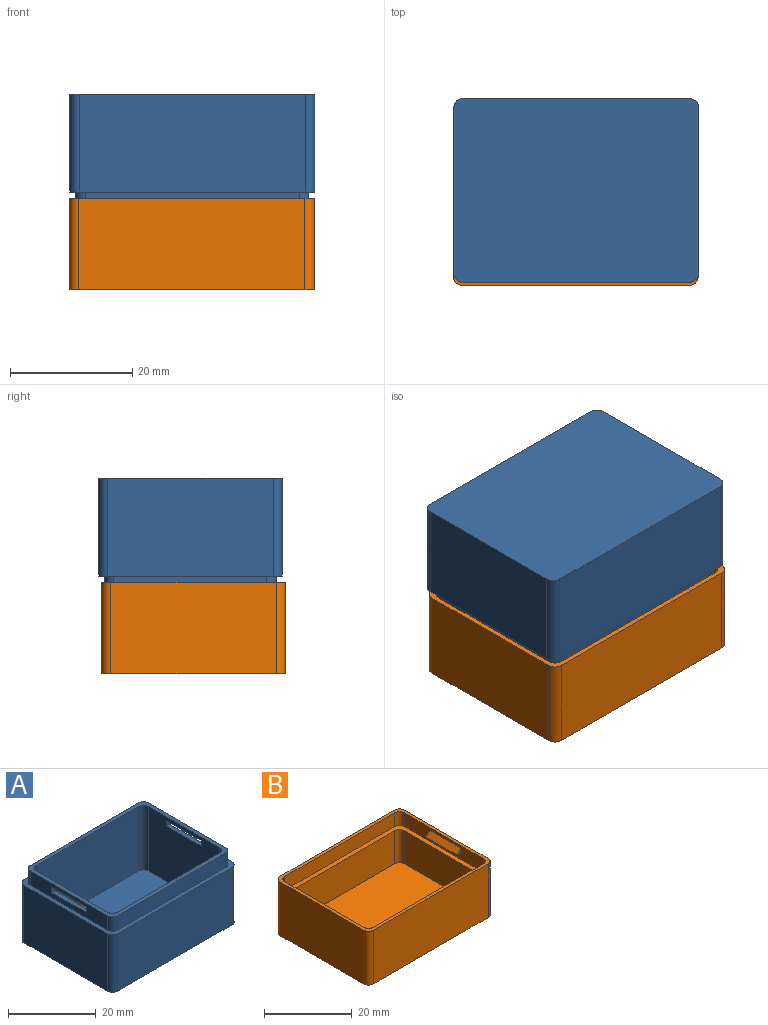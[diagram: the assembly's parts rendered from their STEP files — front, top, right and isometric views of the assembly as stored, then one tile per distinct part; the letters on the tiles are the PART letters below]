
ASSEMBLY  parts=2 mates=1
PART A: 36 faces, bbox 40x30x20 mm
  f0: plane 23x18mm, normal (1,0,0), area 397.5mm2, adj f4,f7,f10,f11,f32,f33,f34,f35
  f1: plane 23x18mm, normal (-1,0,0), area 397.5mm2, adj f4,f7,f8,f9,f28,f29,f30,f31
  f2: plane 25x4mm, normal (-1,0,0), area 83.5mm2, adj f4,f14,f24,f27,f32,f33,f34,f35
  f3: plane 25x4mm, normal (1,0,0), area 83.5mm2, adj f4,f14,f25,f26,f28,f29,f30,f31
  f4: plane 38x28mm, normal (0,0,1), area 128mm2, adj f0,f1,f2,f3,f5,f6,f8,f9
  f5: plane 33x18mm, normal (0,-1,0), area 594mm2, adj f4,f7,f9,f11
  f6: plane 33x18mm, normal (0,1,0), area 594mm2, adj f4,f7,f8,f10
  f7: plane 36x26mm, normal (0,0,1), area 934.1mm2, adj f0,f1,f5,f6,f8,f9,f10,f11
  f8: cylinder r=1.5mm len=18mm, axis (0,0,-1), area 42.4mm2, adj f1,f4,f6,f7
  f9: cylinder r=1.5mm len=18mm, axis (0,0,1), area 42.4mm2, adj f1,f4,f5,f7
  f10: cylinder r=1.5mm len=18mm, axis (0,0,1), area 42.4mm2, adj f0,f4,f6,f7
  f11: cylinder r=1.5mm len=18mm, axis (0,0,-1), area 42.4mm2, adj f0,f4,f5,f7
  f12: plane 35x4mm, normal (0,1,0), area 140mm2, adj f4,f14,f24,f25
  f13: plane 35x4mm, normal (0,-1,0), area 140mm2, adj f4,f14,f26,f27
  f14: plane 40x30mm, normal (0,0,1), area 136mm2, adj f2,f3,f12,f13,f16,f17,f18,f19
  f15: plane 40x30mm, normal (0,0,-1), area 1198.1mm2, adj f16,f17,f18,f19,f20,f21,f22,f23
  f16: cylinder r=1.5mm len=16mm, axis (0,0,1), area 37.7mm2, adj f14,f15,f18,f20
  f17: cylinder r=1.5mm len=16mm, axis (0,0,-1), area 37.7mm2, adj f14,f15,f18,f23
  f18: plane 27x16mm, normal (1,0,0), area 432mm2, adj f14,f15,f16,f17
  f19: cylinder r=1.5mm len=16mm, axis (0,0,-1), area 37.7mm2, adj f14,f15,f20,f22
  f20: plane 37x16mm, normal (0,-1,0), area 592mm2, adj f14,f15,f16,f19
  f21: cylinder r=1.5mm len=16mm, axis (0,0,1), area 37.7mm2, adj f14,f15,f22,f23
  f22: plane 27x16mm, normal (-1,0,0), area 432mm2, adj f14,f15,f19,f21
  f23: plane 37x16mm, normal (0,1,0), area 592mm2, adj f14,f15,f17,f21
  f24: cylinder r=1.5mm len=4mm, axis (0,0,-1), area 9.4mm2, adj f2,f4,f12,f14
  f25: cylinder r=1.5mm len=4mm, axis (0,0,1), area 9.4mm2, adj f3,f4,f12,f14
  f26: cylinder r=1.5mm len=4mm, axis (0,0,-1), area 9.4mm2, adj f3,f4,f13,f14
  f27: cylinder r=1.5mm len=4mm, axis (0,0,1), area 9.4mm2, adj f2,f4,f13,f14
  f28: plane 1.5x1mm, normal (0,-1,0), area 1.5mm2, adj f1,f3,f29,f31
  f29: plane 11x1mm, normal (0,0,1), area 11mm2, adj f1,f3,f28,f30
  f30: plane 1.5x1mm, normal (0,1,0), area 1.5mm2, adj f1,f3,f29,f31
  f31: plane 11x1mm, normal (0,0,-1), area 11mm2, adj f1,f3,f28,f30
  f32: plane 11x1mm, normal (0,0,-1), area 11mm2, adj f0,f2,f33,f35
  f33: plane 1.5x1mm, normal (0,1,0), area 1.5mm2, adj f0,f2,f32,f34
  f34: plane 11x1mm, normal (0,0,1), area 11mm2, adj f0,f2,f33,f35
  f35: plane 1.5x1mm, normal (0,-1,0), area 1.5mm2, adj f0,f2,f32,f34
PART B: 36 faces, bbox 40x30x15 mm
  f0: plane 25.4x3.8mm, normal (-1,0,0), area 83.5mm2, adj f2,f12,f26,f27,f32,f33,f34,f35
  f1: plane 25.4x3.8mm, normal (1,0,0), area 83.5mm2, adj f2,f12,f24,f25,f28,f29,f30,f31
  f2: plane 40x30mm, normal (0,0,1), area 109.4mm2, adj f0,f1,f3,f4,f5,f6,f8,f9
  f3: plane 37x15mm, normal (0,1,0), area 555mm2, adj f2,f7,f8,f11
  f4: plane 27x15mm, normal (-1,0,0), area 405mm2, adj f2,f7,f8,f9
  f5: plane 37x15mm, normal (0,-1,0), area 555mm2, adj f2,f7,f9,f10
  f6: plane 27x15mm, normal (1,0,0), area 405mm2, adj f2,f7,f10,f11
  f7: plane 40x30mm, normal (0,0,-1), area 1198.1mm2, adj f3,f4,f5,f6,f8,f9,f10,f11
  f8: cylinder r=1.5mm len=15mm, axis (0,0,1), area 35.3mm2, adj f2,f3,f4,f7
  f9: cylinder r=1.5mm len=15mm, axis (0,0,-1), area 35.3mm2, adj f2,f4,f5,f7
  f10: cylinder r=1.5mm len=15mm, axis (0,0,1), area 35.3mm2, adj f2,f5,f6,f7
  f11: cylinder r=1.5mm len=15mm, axis (0,0,-1), area 35.3mm2, adj f2,f3,f6,f7
  f12: plane 38.4x28.4mm, normal (0,0,1), area 154.6mm2, adj f0,f1,f13,f14,f16,f17,f18,f19
  f13: plane 35.4x3.8mm, normal (0,-1,0), area 134.5mm2, adj f2,f12,f24,f27
  f14: plane 35.4x3.8mm, normal (0,1,0), area 134.5mm2, adj f2,f12,f25,f26
  f15: plane 36x26mm, normal (0,0,1), area 934.1mm2, adj f16,f17,f18,f19,f20,f21,f22,f23
  f16: cylinder r=1.5mm len=9.2mm, axis (0,0,-1), area 21.7mm2, adj f12,f15,f18,f20
  f17: cylinder r=1.5mm len=9.2mm, axis (0,0,1), area 21.7mm2, adj f12,f15,f18,f23
  f18: plane 23x9.2mm, normal (-1,0,0), area 211.6mm2, adj f12,f15,f16,f17
  f19: cylinder r=1.5mm len=9.2mm, axis (0,0,1), area 21.7mm2, adj f12,f15,f20,f22
  f20: plane 33x9.2mm, normal (0,1,0), area 303.6mm2, adj f12,f15,f16,f19
  f21: cylinder r=1.5mm len=9.2mm, axis (0,0,-1), area 21.7mm2, adj f12,f15,f22,f23
  f22: plane 23x9.2mm, normal (1,0,0), area 211.6mm2, adj f12,f15,f19,f21
  f23: plane 33x9.2mm, normal (0,-1,0), area 303.6mm2, adj f12,f15,f17,f21
  f24: cylinder r=1.5mm len=3.8mm, axis (0,0,1), area 9mm2, adj f1,f2,f12,f13
  f25: cylinder r=1.5mm len=3.8mm, axis (0,0,-1), area 9mm2, adj f1,f2,f12,f14
  f26: cylinder r=1.5mm len=3.8mm, axis (0,0,1), area 9mm2, adj f0,f2,f12,f14
  f27: cylinder r=1.5mm len=3.8mm, axis (0,0,-1), area 9mm2, adj f0,f2,f12,f13
  f28: plane 10x1.3mm, normal (0.73,0,0.68), area 17.7mm2, adj f1,f29,f30,f31
  f29: plane 10x1.2mm, normal (0,0,-1), area 12mm2, adj f1,f28,f30,f31
  f30: plane 1.3x1.2mm, normal (0,-1,0), area 0.8mm2, adj f1,f28,f29
  f31: plane 1.3x1.2mm, normal (0,1,0), area 0.8mm2, adj f1,f28,f29
  f32: plane 10x1.2mm, normal (0,0,-1), area 12mm2, adj f0,f33,f34,f35
  f33: plane 10x1.3mm, normal (-0.73,0,0.68), area 17.7mm2, adj f0,f32,f34,f35
  f34: plane 1.3x1.2mm, normal (0,-1,0), area 0.8mm2, adj f0,f32,f33
  f35: plane 1.3x1.2mm, normal (0,1,0), area 0.8mm2, adj f0,f32,f33
PLACE A rot(axis=(1,0,0),180deg) t=(-64.91,-18.01,30.57)mm
PLACE B rot(axis=(0,0,1),180deg) t=(-15.01,-18.51,-1.43)mm
MATE fastened B.f29 <-> A.f31  axis (0,0,-1) through (-21.41,1.99,11.57)mm
